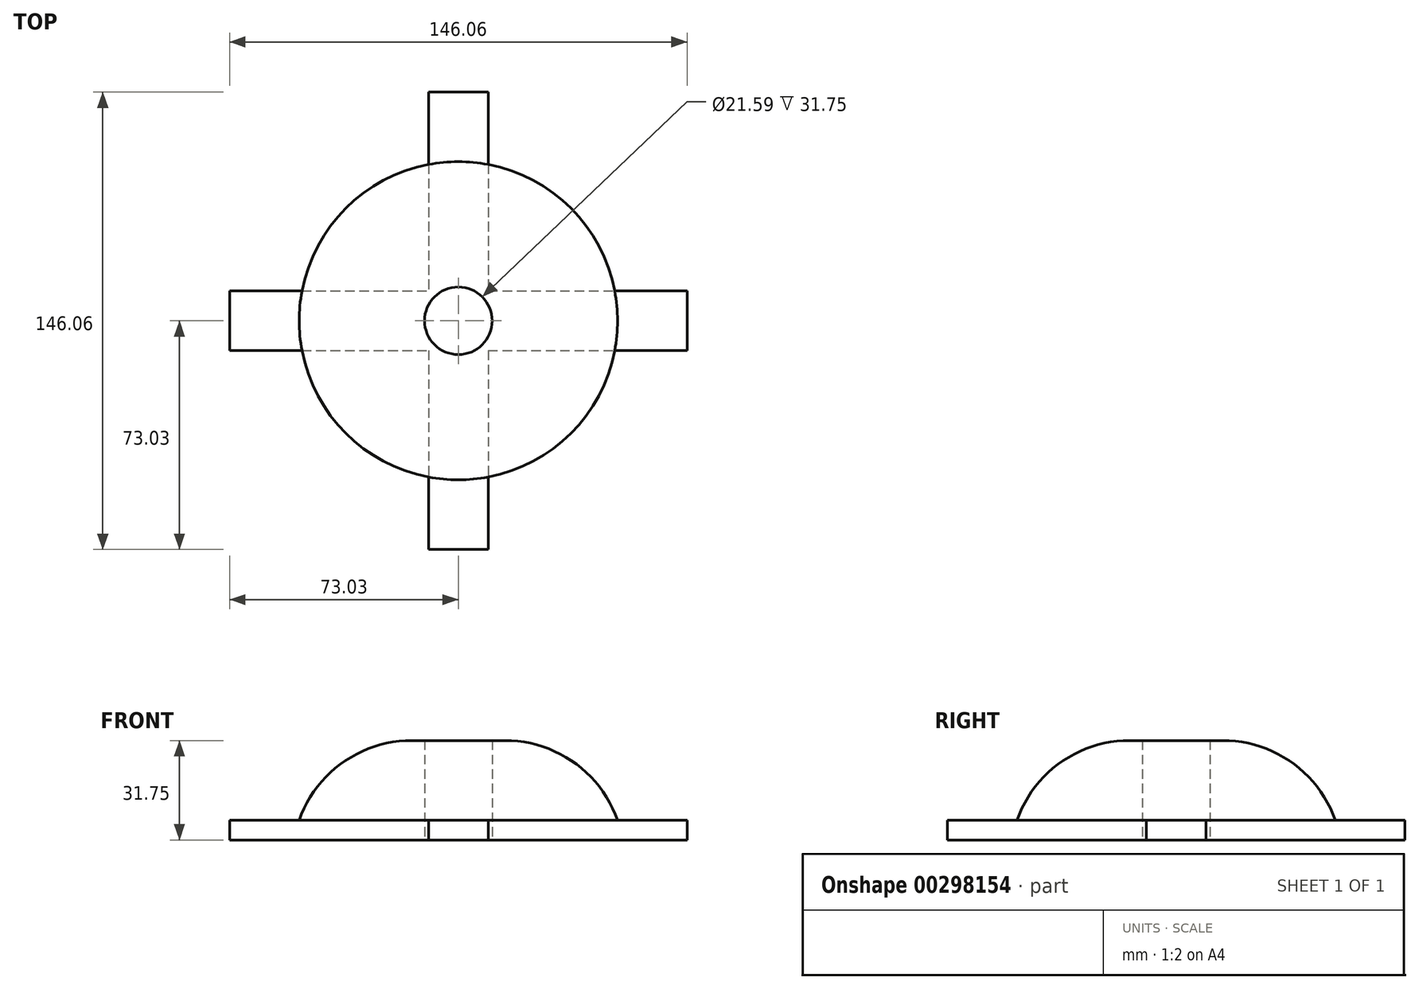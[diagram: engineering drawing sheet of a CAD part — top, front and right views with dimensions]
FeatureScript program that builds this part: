
annotation { "Feature Type Name" : "Feature", "Feature Type Description" : "" }
export const myFeature = defineFeature(function(context is Context, id is Id, definition is map)
    precondition{}
    {
        {
            var Q0;
            Q0=qCreatedBy(makeId("Top.planeOp"),FACE);
            var sketch = newSketch(context, id + "F0", { "sketchPlane" : qUnion([Q0])});
            skLineSegment(sketch, "E0.bottom", {"start": v(-73.03, -9.53) * mm, "end": v(73.03, -9.53) * mm});
            skLineSegment(sketch, "E0.top", {"start": v(-73.03, 9.53) * mm, "end": v(73.03, 9.53) * mm});
            skLineSegment(sketch, "E0.left", {"start": v(-73.03, -9.53) * mm, "end": v(-73.03, 9.53) * mm});
            skLineSegment(sketch, "E0.right", {"start": v(73.03, -9.53) * mm, "end": v(73.03, 9.53) * mm});
            skPoint(sketch, "E0.middle", {"position": v(0, 0) * mm});
            skLineSegment(sketch, "E1.bottom", {"start": v(-9.53, 73.03) * mm, "end": v(9.53, 73.03) * mm});
            skLineSegment(sketch, "E1.top", {"start": v(-9.53, -73.03) * mm, "end": v(9.52, -73.03) * mm});
            skLineSegment(sketch, "E1.left", {"start": v(-9.53, 73.03) * mm, "end": v(-9.53, -73.03) * mm});
            skLineSegment(sketch, "E1.right", {"start": v(9.53, 73.03) * mm, "end": v(9.52, -73.03) * mm});
            skSolve(sketch);
        }
        {
            var Q0;
            {var subQ5=sQuery(id+"F0.wireOp",EDGE,"E1.bottom");Q0=makeQuery(id+"F0.imprint","IMPRINT",FACE,{"disambiguationData":[TD([[makeQuery(id+"F0.imprint","IMPRINT",EDGE,{"derivedFrom":subQ5}),-1.0]])]});}
            var Q1;
            {var subQ0=sQuery(id+"F0.wireOp",EDGE,"E0.left");Q1=makeQuery(id+"F0.imprint","IMPRINT",FACE,{"disambiguationData":[TD([[makeQuery(id+"F0.imprint","IMPRINT",EDGE,{"derivedFrom":subQ0}),-1.0]])]});}
            var Q2;
            {var subQ0=sQuery(id+"F0.wireOp",EDGE,"E1.left");var subQ1=sQuery(id+"F0.wireOp",EDGE,"E0.bottom");var subQ2=makeQuery(id+"F0.imprint","INTERSECT",VERTEX,{"derivedFrom":[subQ1,subQ0]});Q2=makeQuery(id+"F0.imprint","IMPRINT",FACE,{"disambiguationData":[TD([[makeQuery(id+"F0.imprint","IMPRINT",EDGE,{"disambiguationData":[TD([[subQ2,-1.0]])],"derivedFrom":subQ1}),1.0]])]});}
            var Q3;
            {var subQ0=sQuery(id+"F0.wireOp",EDGE,"E0.right");Q3=makeQuery(id+"F0.imprint","IMPRINT",FACE,{"disambiguationData":[TD([[makeQuery(id+"F0.imprint","IMPRINT",EDGE,{"derivedFrom":subQ0}),1.0]])]});}
            var Q4;
            {var subQ5=sQuery(id+"F0.wireOp",EDGE,"E1.top");Q4=makeQuery(id+"F0.imprint","IMPRINT",FACE,{"disambiguationData":[TD([[makeQuery(id+"F0.imprint","IMPRINT",EDGE,{"derivedFrom":subQ5}),1.0]])]});}
            extrude(context, id + "F1", {"entities" : qUnion([Q0, Q1, Q2, Q3, Q4]), "depth" : 6.35 * mm});
        }
        {
            var Q0;
            Q0=makeQuery(id+"F1.opExtrude","CAP_FACE",FACE,{"disambiguationData":[OSD([sQuery(id+"F0.wireOp",EDGE,"E0.bottom"),sQuery(id+"F0.wireOp",EDGE,"E0.top"),sQuery(id+"F0.wireOp",EDGE,"E0.left"),sQuery(id+"F0.wireOp",EDGE,"E0.right"),sQuery(id+"F0.wireOp",EDGE,"E1.bottom"),sQuery(id+"F0.wireOp",EDGE,"E1.top"),sQuery(id+"F0.wireOp",EDGE,"E1.left"),sQuery(id+"F0.wireOp",EDGE,"E1.right")])],"isStart":false});
            var sketch = newSketch(context, id + "F2", { "sketchPlane" : qUnion([Q0])});
            skCircle(sketch, "E2", {"center": v(0, 0) * mm, "radius": 50.8 * mm});
            skCircle(sketch, "E3", {"center": v(0, 0) * mm, "radius": 10.8 * mm});
            skSolve(sketch);
        }
        {
            var Q0;
            Q0=makeQuery(id+"F2.imprint","IMPRINT",FACE,{"disambiguationData":[TD([[makeQuery(id+"F2.imprint","IMPRINT",EDGE,{"derivedFrom":sQuery(id+"F2.wireOp",EDGE,"E3")}),-1.0]])]});
            var Q1;
            {var subQ0=sQuery(id+"F2.wireOp",EDGE,"E2");var subQ1=sQuery(id+"F0.wireOp",EDGE,"E0.bottom");var subQ4=makeQuery(id+"F1.opExtrude","CAP_EDGE",EDGE,{"disambiguationData":[OSD([subQ1]),TDD([makeQuery(id+"F0.imprint","IMPRINT",EDGE,{"disambiguationData":[TD([[makeQuery(id+"F0.imprint","INTERSECT",VERTEX,{"derivedFrom":[subQ1,sQuery(id+"F0.wireOp",EDGE,"E0.left")]}),-1.0]])],"derivedFrom":subQ1})])],"isStart":false});var subQ5=makeQuery(id+"F2.imprint","INTERSECT",VERTEX,{"derivedFrom":[subQ4,subQ0]});Q1=makeQuery(id+"F2.imprint","IMPRINT",FACE,{"disambiguationData":[TD([[makeQuery(id+"F2.imprint","IMPRINT",EDGE,{"disambiguationData":[TD([[subQ5,-1.0]])],"derivedFrom":subQ0}),1.0]])]});}
            var Q2;
            {var subQ0=sQuery(id+"F2.wireOp",EDGE,"E2");var subQ1=sQuery(id+"F0.wireOp",EDGE,"E1.left");var subQ4=makeQuery(id+"F1.opExtrude","CAP_EDGE",EDGE,{"disambiguationData":[OSD([subQ1]),TDD([makeQuery(id+"F0.imprint","IMPRINT",EDGE,{"disambiguationData":[TD([[makeQuery(id+"F0.imprint","INTERSECT",VERTEX,{"derivedFrom":[sQuery(id+"F0.wireOp",EDGE,"E1.bottom"),subQ1]}),-1.0]])],"derivedFrom":subQ1})])],"isStart":false});var subQ5=makeQuery(id+"F2.imprint","INTERSECT",VERTEX,{"derivedFrom":[subQ4,subQ0]});Q2=makeQuery(id+"F2.imprint","IMPRINT",FACE,{"disambiguationData":[TD([[makeQuery(id+"F2.imprint","IMPRINT",EDGE,{"disambiguationData":[TD([[subQ5,-1.0]])],"derivedFrom":subQ0}),1.0]])]});}
            var Q3;
            {var subQ0=sQuery(id+"F2.wireOp",EDGE,"E2");var subQ1=sQuery(id+"F0.wireOp",EDGE,"E1.right");var subQ4=makeQuery(id+"F1.opExtrude","CAP_EDGE",EDGE,{"disambiguationData":[OSD([subQ1]),TDD([makeQuery(id+"F0.imprint","IMPRINT",EDGE,{"disambiguationData":[TD([[makeQuery(id+"F0.imprint","INTERSECT",VERTEX,{"derivedFrom":[sQuery(id+"F0.wireOp",EDGE,"E1.bottom"),subQ1]}),-1.0]])],"derivedFrom":subQ1})])],"isStart":false});var subQ5=makeQuery(id+"F2.imprint","INTERSECT",VERTEX,{"derivedFrom":[subQ4,subQ0]});Q3=makeQuery(id+"F2.imprint","IMPRINT",FACE,{"disambiguationData":[TD([[makeQuery(id+"F2.imprint","IMPRINT",EDGE,{"disambiguationData":[TD([[subQ5,1.0]])],"derivedFrom":subQ0}),1.0]])]});}
            var Q4;
            {var subQ0=sQuery(id+"F2.wireOp",EDGE,"E2");var subQ1=sQuery(id+"F0.wireOp",EDGE,"E1.right");var subQ4=makeQuery(id+"F1.opExtrude","CAP_EDGE",EDGE,{"disambiguationData":[OSD([subQ1]),TDD([makeQuery(id+"F0.imprint","IMPRINT",EDGE,{"disambiguationData":[TD([[makeQuery(id+"F0.imprint","INTERSECT",VERTEX,{"derivedFrom":[sQuery(id+"F0.wireOp",EDGE,"E1.top"),subQ1]}),1.0]])],"derivedFrom":subQ1})])],"isStart":false});var subQ5=makeQuery(id+"F2.imprint","INTERSECT",VERTEX,{"derivedFrom":[subQ4,subQ0]});Q4=makeQuery(id+"F2.imprint","IMPRINT",FACE,{"disambiguationData":[TD([[makeQuery(id+"F2.imprint","IMPRINT",EDGE,{"disambiguationData":[TD([[subQ5,-1.0]])],"derivedFrom":subQ0}),1.0]])]});}
            extrude(context, id + "F3", {"entities" : qUnion([Q0, Q1, Q2, Q3, Q4]), "operationType" : NewBodyOperationType.ADD, "depth" : 25.4 * mm});
        }
        {
            var Q0;
            Q0=makeQuery(id+"F3.boolean.opBoolean","SPLIT",FACE,{"disambiguationData":[TD([makeQuery(id+"F3.opExtrude","SWEPT_FACE",FACE,{"disambiguationData":[OSD([sQuery(id+"F2.wireOp",EDGE,"E3")])]})])],"derivedFrom":makeQuery(id+"F1.opExtrude","CAP_FACE",FACE,{"disambiguationData":[OSD([sQuery(id+"F0.wireOp",EDGE,"E0.bottom"),sQuery(id+"F0.wireOp",EDGE,"E0.top"),sQuery(id+"F0.wireOp",EDGE,"E0.left"),sQuery(id+"F0.wireOp",EDGE,"E0.right"),sQuery(id+"F0.wireOp",EDGE,"E1.bottom"),sQuery(id+"F0.wireOp",EDGE,"E1.top"),sQuery(id+"F0.wireOp",EDGE,"E1.left"),sQuery(id+"F0.wireOp",EDGE,"E1.right")])],"isStart":false})});
            extrude(context, id + "F4", {"entities" : qUnion([Q0]), "operationType" : NewBodyOperationType.REMOVE, "endBound" : BoundingType.UP_TO_NEXT, "oppositeDirection" : true, "depth" : 25.4 * mm});
        }
        {
            var Q0;
            Q0=makeQuery(id+"F3.opExtrude","CAP_EDGE",EDGE,{"disambiguationData":[OSD([sQuery(id+"F2.wireOp",EDGE,"E2")])],"isStart":false});
            fillet(context, id + "F5", {"entities" : qUnion([Q0]), "radius" : 38.1 * mm, "tangentPropagation" : true, "allowEdgeOverflow" : false});
        }
    });
